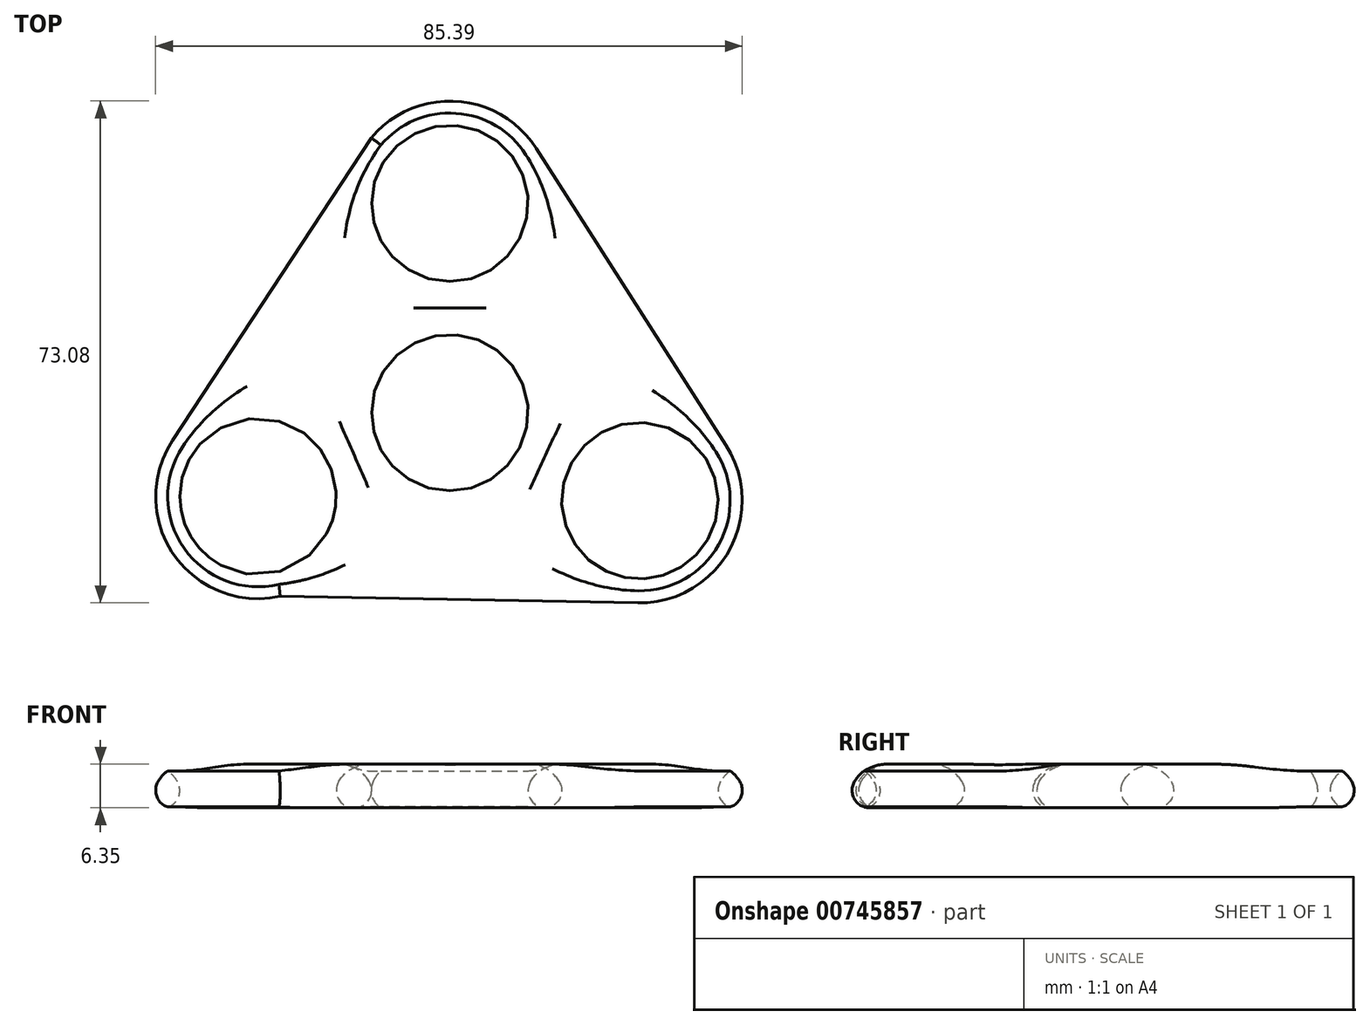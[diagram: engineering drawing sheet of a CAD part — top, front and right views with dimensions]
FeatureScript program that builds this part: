
annotation { "Feature Type Name" : "Feature", "Feature Type Description" : "" }
export const myFeature = defineFeature(function(context is Context, id is Id, definition is map)
    precondition{}
    {
        {
            var Q0;
            Q0=qCreatedBy(makeId("Top.planeOp"),FACE);
            var sketch = newSketch(context, id + "F0", { "sketchPlane" : qUnion([Q0])});
            skCircle(sketch, "E0", {"center": v(0, 0) * mm, "radius": 11.05 * mm});
            skCircle(sketch, "E1", {"center": v(0, 0) * mm, "radius": 13.97 * mm});
            skLineSegment(sketch, "E2", {"start": v(0, 0) * mm, "end": v(0, 30.48) * mm});
            skLineSegment(sketch, "E3", {"start": v(0, 0) * mm, "end": v(27.66, -12.8) * mm});
            skLineSegment(sketch, "E4", {"start": v(27.66, -12.8) * mm, "end": v(0, 0) * mm});
            skLineSegment(sketch, "E5", {"start": v(0, 0) * mm, "end": v(-27.93, -12.2) * mm});
            skCircle(sketch, "E6", {"center": v(0, 30.48) * mm, "radius": 11.05 * mm});
            skCircle(sketch, "E7", {"center": v(0, 30.48) * mm, "radius": 15.24 * mm});
            skCircle(sketch, "E8", {"center": v(27.66, -12.8) * mm, "radius": 11.05 * mm});
            skCircle(sketch, "E9", {"center": v(27.66, -12.8) * mm, "radius": 15.24 * mm});
            skCircle(sketch, "E10", {"center": v(-27.93, -12.2) * mm, "radius": 11.05 * mm});
            skCircle(sketch, "E11", {"center": v(-27.93, -12.2) * mm, "radius": 15.24 * mm});
            skLineSegment(sketch, "E12", {"start": v(-11.72, 40.23) * mm, "end": v(-40.67, -3.84) * mm});
            skLineSegment(sketch, "E13", {"start": v(12.83, 38.7) * mm, "end": v(40.5, -4.6) * mm});
            skLineSegment(sketch, "E14", {"start": v(-24.66, -27.1) * mm, "end": v(27.38, -28.04) * mm});
            skSolve(sketch);
        }
        {
            var Q0;
            {var subQ0=sQuery(id+"F0.wireOp",EDGE,"E13");Q0=makeQuery(id+"F0.imprint","IMPRINT",FACE,{"disambiguationData":[TD([[makeQuery(id+"F0.imprint","IMPRINT",EDGE,{"derivedFrom":subQ0}),-1.0]])]});}
            var Q1;
            Q1=makeQuery(id+"F0.imprint","IMPRINT",FACE,{"disambiguationData":[TD([[makeQuery(id+"F0.imprint","IMPRINT",EDGE,{"derivedFrom":sQuery(id+"F0.wireOp",EDGE,"E6")}),-1.0]])]});
            var Q2;
            {var subQ0=sQuery(id+"F0.wireOp",EDGE,"E2");var subQ1=sQuery(id+"F0.wireOp",EDGE,"E0");var subQ2=makeQuery(id+"F0.imprint","INTERSECT",VERTEX,{"derivedFrom":[subQ1,subQ0]});Q2=makeQuery(id+"F0.imprint","IMPRINT",FACE,{"disambiguationData":[TD([[makeQuery(id+"F0.imprint","IMPRINT",EDGE,{"disambiguationData":[TD([[subQ2,1.0]])],"derivedFrom":subQ1}),-1.0]])]});}
            var Q3;
            {var subQ0=sQuery(id+"F0.wireOp",EDGE,"E5");var subQ1=sQuery(id+"F0.wireOp",EDGE,"E0");var subQ2=makeQuery(id+"F0.imprint","INTERSECT",VERTEX,{"derivedFrom":[subQ1,subQ0]});Q3=makeQuery(id+"F0.imprint","IMPRINT",FACE,{"disambiguationData":[TD([[makeQuery(id+"F0.imprint","IMPRINT",EDGE,{"disambiguationData":[TD([[subQ2,1.0]])],"derivedFrom":subQ1}),-1.0]])]});}
            var Q4;
            {var subQ0=sQuery(id+"F0.wireOp",EDGE,"E5");var subQ1=sQuery(id+"F0.wireOp",EDGE,"E0");var subQ2=makeQuery(id+"F0.imprint","INTERSECT",VERTEX,{"derivedFrom":[subQ1,subQ0]});Q4=makeQuery(id+"F0.imprint","IMPRINT",FACE,{"disambiguationData":[TD([[makeQuery(id+"F0.imprint","IMPRINT",EDGE,{"disambiguationData":[TD([[subQ2,-1.0]])],"derivedFrom":subQ1}),-1.0]])]});}
            var Q5;
            {var subQ0=sQuery(id+"F0.wireOp",EDGE,"E14");Q5=makeQuery(id+"F0.imprint","IMPRINT",FACE,{"disambiguationData":[TD([[makeQuery(id+"F0.imprint","IMPRINT",EDGE,{"derivedFrom":subQ0}),1.0]])]});}
            var Q6;
            Q6=makeQuery(id+"F0.imprint","IMPRINT",FACE,{"disambiguationData":[TD([[makeQuery(id+"F0.imprint","IMPRINT",EDGE,{"derivedFrom":sQuery(id+"F0.wireOp",EDGE,"E8")}),-1.0]])]});
            var Q7;
            {var subQ1=sQuery(id+"F0.wireOp",EDGE,"E5");var subQ3=sQuery(id+"F0.wireOp",EDGE,"E1");var subQ4=makeQuery(id+"F0.imprint","INTERSECT",VERTEX,{"derivedFrom":[subQ3,subQ1]});Q7=makeQuery(id+"F0.imprint","IMPRINT",FACE,{"disambiguationData":[TD([[makeQuery(id+"F0.imprint","IMPRINT",EDGE,{"disambiguationData":[TD([[subQ4,1.0]])],"derivedFrom":subQ3}),-1.0]])]});}
            var Q8;
            Q8=makeQuery(id+"F0.imprint","IMPRINT",FACE,{"disambiguationData":[TD([[makeQuery(id+"F0.imprint","IMPRINT",EDGE,{"derivedFrom":sQuery(id+"F0.wireOp",EDGE,"E10")}),-1.0]])]});
            extrude(context, id + "F1", {"entities" : qUnion([Q0, Q1, Q2, Q3, Q4, Q5, Q6, Q7, Q8]), "depth" : 6.35 * mm, "offsetDistance" : 25.4 * mm});
        }
        {
            var Q0;
            Q0=makeQuery(id+"F1.opExtrude","CAP_EDGE",EDGE,{"disambiguationData":[OSD([sQuery(id+"F0.wireOp",EDGE,"E0")])],"isStart":false});
            var Q1;
            Q1=makeQuery(id+"F1.opExtrude","CAP_EDGE",EDGE,{"disambiguationData":[OSD([sQuery(id+"F0.wireOp",EDGE,"E10")])],"isStart":false});
            var Q2;
            Q2=makeQuery(id+"F1.opExtrude","CAP_EDGE",EDGE,{"disambiguationData":[OSD([sQuery(id+"F0.wireOp",EDGE,"E6")])],"isStart":false});
            var Q3;
            Q3=makeQuery(id+"F1.opExtrude","CAP_EDGE",EDGE,{"disambiguationData":[OSD([sQuery(id+"F0.wireOp",EDGE,"E8")])],"isStart":false});
            var Q4;
            Q4=makeQuery(id+"F1.opExtrude","CAP_FACE",FACE,{"disambiguationData":[OSD([sQuery(id+"F0.wireOp",EDGE,"E0"),sQuery(id+"F0.wireOp",EDGE,"E6"),sQuery(id+"F0.wireOp",EDGE,"E7"),sQuery(id+"F0.wireOp",EDGE,"E8"),sQuery(id+"F0.wireOp",EDGE,"E9"),sQuery(id+"F0.wireOp",EDGE,"E10"),sQuery(id+"F0.wireOp",EDGE,"E11"),sQuery(id+"F0.wireOp",EDGE,"E12"),sQuery(id+"F0.wireOp",EDGE,"E13"),sQuery(id+"F0.wireOp",EDGE,"E14")])],"isStart":false});
            fillet(context, id + "F2", {"entities" : qUnion([Q0, Q1, Q2, Q3, Q4]), "radius" : 5.08 * mm, "tangentPropagation" : true, "allowEdgeOverflow" : false});
        }
        {
            var Q0;
            Q0=makeQuery(id+"F1.opExtrude","CAP_FACE",FACE,{"disambiguationData":[OSD([sQuery(id+"F0.wireOp",EDGE,"E0"),sQuery(id+"F0.wireOp",EDGE,"E6"),sQuery(id+"F0.wireOp",EDGE,"E7"),sQuery(id+"F0.wireOp",EDGE,"E8"),sQuery(id+"F0.wireOp",EDGE,"E9"),sQuery(id+"F0.wireOp",EDGE,"E10"),sQuery(id+"F0.wireOp",EDGE,"E11"),sQuery(id+"F0.wireOp",EDGE,"E12"),sQuery(id+"F0.wireOp",EDGE,"E13"),sQuery(id+"F0.wireOp",EDGE,"E14")])],"isStart":true});
            fillet(context, id + "F3", {"entities" : qUnion([Q0]), "radius" : 2.54 * mm, "tangentPropagation" : true, "allowEdgeOverflow" : false});
        }
    });
